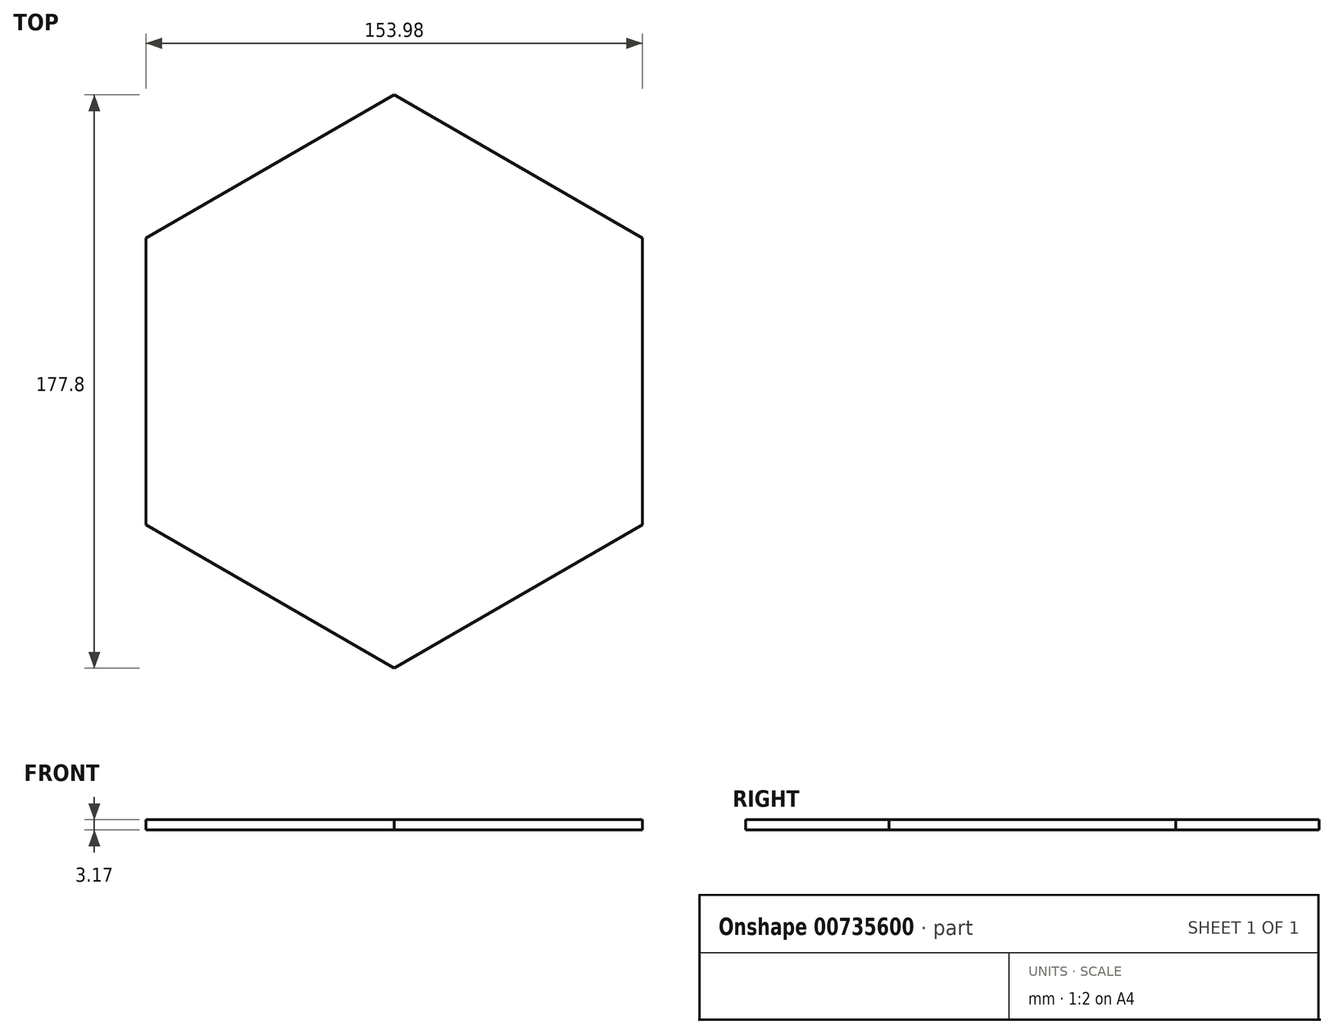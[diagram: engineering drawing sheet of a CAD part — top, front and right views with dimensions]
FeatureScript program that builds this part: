
annotation { "Feature Type Name" : "Feature", "Feature Type Description" : "" }
export const myFeature = defineFeature(function(context is Context, id is Id, definition is map)
    precondition{}
    {
        {
            var Q0;
            Q0=qCreatedBy(makeId("Top.planeOp"),FACE);
            var sketch = newSketch(context, id + "F0", { "sketchPlane" : qUnion([Q0])});
            skLineSegment(sketch, "E0", {"start": v(0, 0) * mm, "end": v(0, 88.9) * mm});
            skLineSegment(sketch, "E1", {"start": v(0, 0) * mm, "end": v(0, -88.9) * mm});
            skCircle(sketch, "E2.cCircle", {"center": v(0, 0) * mm, "radius": 88.9 * mm, "construction": true});
            skLineSegment(sketch, "E2.0", {"start": v(0, 88.9) * mm, "end": v(76.99, 44.45) * mm});
            skLineSegment(sketch, "E2.1", {"start": v(76.99, 44.45) * mm, "end": v(76.99, -44.45) * mm});
            skLineSegment(sketch, "E2.2", {"start": v(76.99, -44.45) * mm, "end": v(0, -88.9) * mm});
            skLineSegment(sketch, "E2.3", {"start": v(0, -88.9) * mm, "end": v(-76.99, -44.45) * mm});
            skLineSegment(sketch, "E2.4", {"start": v(-76.99, -44.45) * mm, "end": v(-76.99, 44.45) * mm});
            skLineSegment(sketch, "E2.5", {"start": v(-76.99, 44.45) * mm, "end": v(0, 88.9) * mm});
            skLineSegment(sketch, "E3", {"start": v(76.99, 0) * mm, "end": v(73.81, 0) * mm});
            skLineSegment(sketch, "E4", {"start": v(73.81, 0) * mm, "end": v(58.57, 0) * mm});
            skLineSegment(sketch, "E5", {"start": v(58.57, 0) * mm, "end": v(55.4, 0) * mm});
            skLineSegment(sketch, "E6", {"start": v(58.57, 0) * mm, "end": v(66.2, 0) * mm});
            skSolve(sketch);
        }
        {
            var Q0;
            Q0=makeQuery(id+"F0.imprint","IMPRINT",FACE,{"disambiguationData":[TD([[makeQuery(id+"F0.imprint","IMPRINT",EDGE,{"derivedFrom":sQuery(id+"F0.wireOp",EDGE,"E0")}),1.0]])]});
            var Q1;
            Q1=makeQuery(id+"F0.imprint","IMPRINT",FACE,{"disambiguationData":[TD([[makeQuery(id+"F0.imprint","IMPRINT",EDGE,{"derivedFrom":sQuery(id+"F0.wireOp",EDGE,"E0")}),-1.0]])]});
            extrude(context, id + "F1", {"entities" : qUnion([Q0, Q1]), "depth" : 3.17 * mm, "offsetDistance" : 25.4 * mm});
        }
    });
